# Revit family: FU_Chair_Sandler_TIMBERLY_2
name_source: partatom
category: Furniture
units: mm (PartAtom-declared; Revit-internal decimal feet)

## family parameters
Always vertical = No
Cut with Voids When Loaded = No
OmniClass Number = 23.21.23.15.17
Room Calculation Point = No
Shared = No
Work Plane-Based = Yes

## types (4) — shared parameters
401D = No
401G = No
BIMobject category = Chair
BIMobject category code = furniture-chair
BIMobject main category = Furniture
BIMobject main category code = furniture
Brand url = https://www.sandlerseating.com
Default Elevation = 1219.2 mm  [stored 4 ft]
Description = Chair
Design country = UK
Edition number = 1
IFC Classification = Furnishing Element
Manufacturer = Sandler
Manufacturer country = UK
Manufacturer name = Sandler
Masterformat 2014 Code = 12 48 43.13
Masterformat 2014 Description = Chair Mats
OmniClass Code = 23-21 23 15 17
Product Guid = ??
Product SKU = ??
Product data url = https://www.sandlerseating.com
Product family = Furniture
Product group = Chair
Shell = TP01 - TIMBERLY
Shell Material = Default
Uniformat II Description = Movable Furnishings
depth = 1040 mm
height = 1165.265 mm
width = 1040 mm

## per-type parameters (varying)
| type | Back Material | Frame | Frame Material | Seat Material |
| TIMBERLY 2.3S | Fabric - Gravity - Sunni CPC20 | BS06 - TIMBERLY | Wood - Beech - Walnut - V | Fabric - Gravity - Sunni CPC20 |
| TIMBERLY 2.3 | Default | BS05 - TIMBERLY | Wood - Beech - Walnut - V | Fabric - Gravity - Frozen CPC27 |
| TIMBERLY 2.1S | Fabric - Gravity - Frost CPC32 | BS06 - TIMBERLY | Wood - Beech - Wenge - V | Fabric - Gravity - Gooseberry CPC07 |
| TIMBERLY 2.1 | Default | BS05 - TIMBERLY | Black RAL9005 | Fabric - Gravity - Frozen CPC27 |

note: column(s) folded — value = type name in every type: Model, Product name

note: [stored X ft] marks values corroborated as IEEE doubles in the binary element streams (Revit-internal decimal feet)

## geometry (parser evidence)
native form markers: Sweep x10
no freeform markers — native parametric forms only
